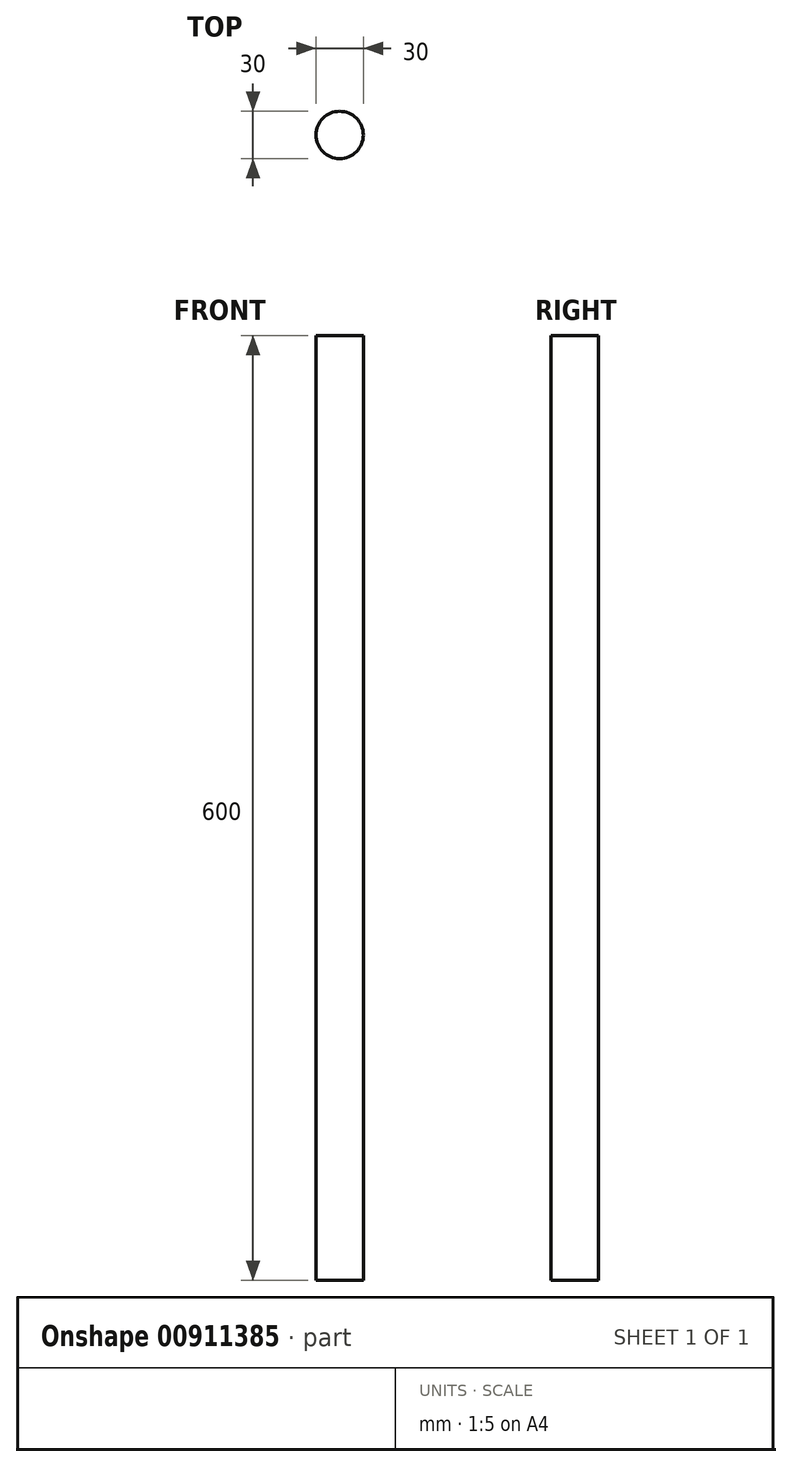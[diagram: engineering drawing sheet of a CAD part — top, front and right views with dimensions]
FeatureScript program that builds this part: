
annotation { "Feature Type Name" : "Feature", "Feature Type Description" : "" }
export const myFeature = defineFeature(function(context is Context, id is Id, definition is map)
    precondition{}
    {
        {
            var Q0;
            Q0=qCreatedBy(makeId("Front.planeOp"),FACE);
            var sketch = newSketch(context, id + "F0", { "sketchPlane" : qUnion([Q0])});
            skLineSegment(sketch, "E0", {"start": v(0, -18.62) * mm, "end": v(0, 58.63) * mm, "construction": true});
            skLineSegment(sketch, "E1", {"start": v(-15, 0) * mm, "end": v(-15, 600) * mm});
            skLineSegment(sketch, "E2", {"start": v(-15, 600) * mm, "end": v(0, 600) * mm});
            skLineSegment(sketch, "E3", {"start": v(-15, 0) * mm, "end": v(0, 0) * mm});
            skLineSegment(sketch, "E4", {"start": v(0, 0) * mm, "end": v(0, 600) * mm});
            skSolve(sketch);
        }
        {
            var Q0;
            Q0=makeQuery(id+"F0.imprint","IMPRINT",FACE,{"disambiguationData":[TD([[makeQuery(id+"F0.imprint","IMPRINT",EDGE,{"derivedFrom":sQuery(id+"F0.wireOp",EDGE,"E1")}),-1.0]])]});
            var Q1;
            Q1=sQuery(id+"F0.wireOp",EDGE,"E4");
            revolve(context, id + "F1", {"surfaceOperationType" : NewSurfaceOperationType.NEW, "entities" : qUnion([Q0]), "axis" : qUnion([Q1]), "revolveType" : RevolveType.FULL});
        }
    });
